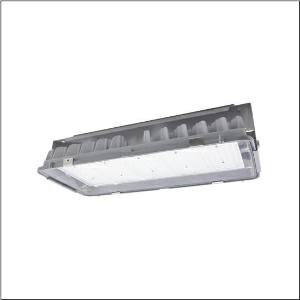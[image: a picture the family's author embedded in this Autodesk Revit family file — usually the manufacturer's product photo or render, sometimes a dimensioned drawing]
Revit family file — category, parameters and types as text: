
# Revit family: highbay_11xtreme_51hf61da4hma
name_source: partatom
category: Lighting Fixtures
units: mm (PartAtom-declared; Revit-internal decimal feet)

## family parameters
Cut with Voids When Loaded = No
Host = Face
Light Source = No
Part Type = Normal
Room Calculation Point = No
Round Connector Dimension = Use Diameter
Shared = No

## types (1)
- --- (1 x LED, 18700 lm, 96.3 W, 4000K)
    Apparent Load = 96 VA
    CIE Flux Codes = 88 96 99 100 100
    Color Rendering = 80
    Color Temperature = 4000K
    Default Elevation = 1800 mm
    Description = Highbay 11Xtreme, LED high bay luminaire, primary light control with lens, of PMMA, primary optical cover: cover, of toughened safety glass, light emission: direct distribution, primary light characteristic: symmetric, installation type: suspended mounting, surface-mounted, 1x LED module,for 1x LED, rated luminous flux: 18.700lm, luminous efficacy: 194lm/W, light colour: 840, colour temperature: 4000K, with cable H07RN-F 5x 1.5mm², mains connection: 220..240V, AC, 50/60Hz, cable length: 1,5m, rated input power: 96W, luminaire housing, of diecast aluminium, coated, silver, length: 595mm, width: 280mm, height: 195mm, protection rating (complete): IP66, insulation class (complete): insulation class I (protective earthing), certification: CE, ENEC, UKCA, protection symbol: D, ball protection: ball impact resistant according to DIN VDE 0710 part 13 (with chain suspension), impact resistance: IK08, permissible operating ambient temperature: -25..+70°C, reducing of maximum allowable ambient temperature of 5°C with ceiling mounting, packaging unit: 1 piece
    Height = 157 mm
    Lamp = 1 x LED
    Lamp Light Flux = 18700 lm
    Lamp Power = 96.3 W
    Lamp count = 1
    Length = 593 mm
    Luminous efficacy = 194 lm/W
    Manufacturer = Siteco
    ModVariant = No
    Model = 51HF61DA4HMA
    Mounting Place = Ceiling
    Mounting Type = Pendant
    Number of Poles = 1
    OnlyDefault = Yes
    Power Factor = 1
    Product Name = Highbay 11Xtreme
    Product group = LED high bay luminaire
    ProductGroupID = 903
    Protection Class = Protection class I
    Protection Degree = IP 66
    RLX_Detail_Level = 1
    RLX_Emergency_Light_Flux = 0 lm
    RLX_Emergency_Type = 0
    RLX_Emergency_Type_DB = No
    RlxData = <blob elided: 27733 chars, md5=646c2d12>
    Socket = socket
    Standby Power = 0 W
    System Light Flux = 18700 lm
    System Power = 96 W
    Type Comments = factory setting: luminous flux: 100 % | dim-lin: 254 | 650 mA
    Type Image = l_1258342.jpg
    URL = http://relux.com
    VarID = @adj_035881
    Voltage = 0 V
    Weight = 0.00 kg
    Width = 278 mm

## geometry (parser evidence)
native form markers: Blend x4, Sweep x9
no freeform markers — native parametric forms only
